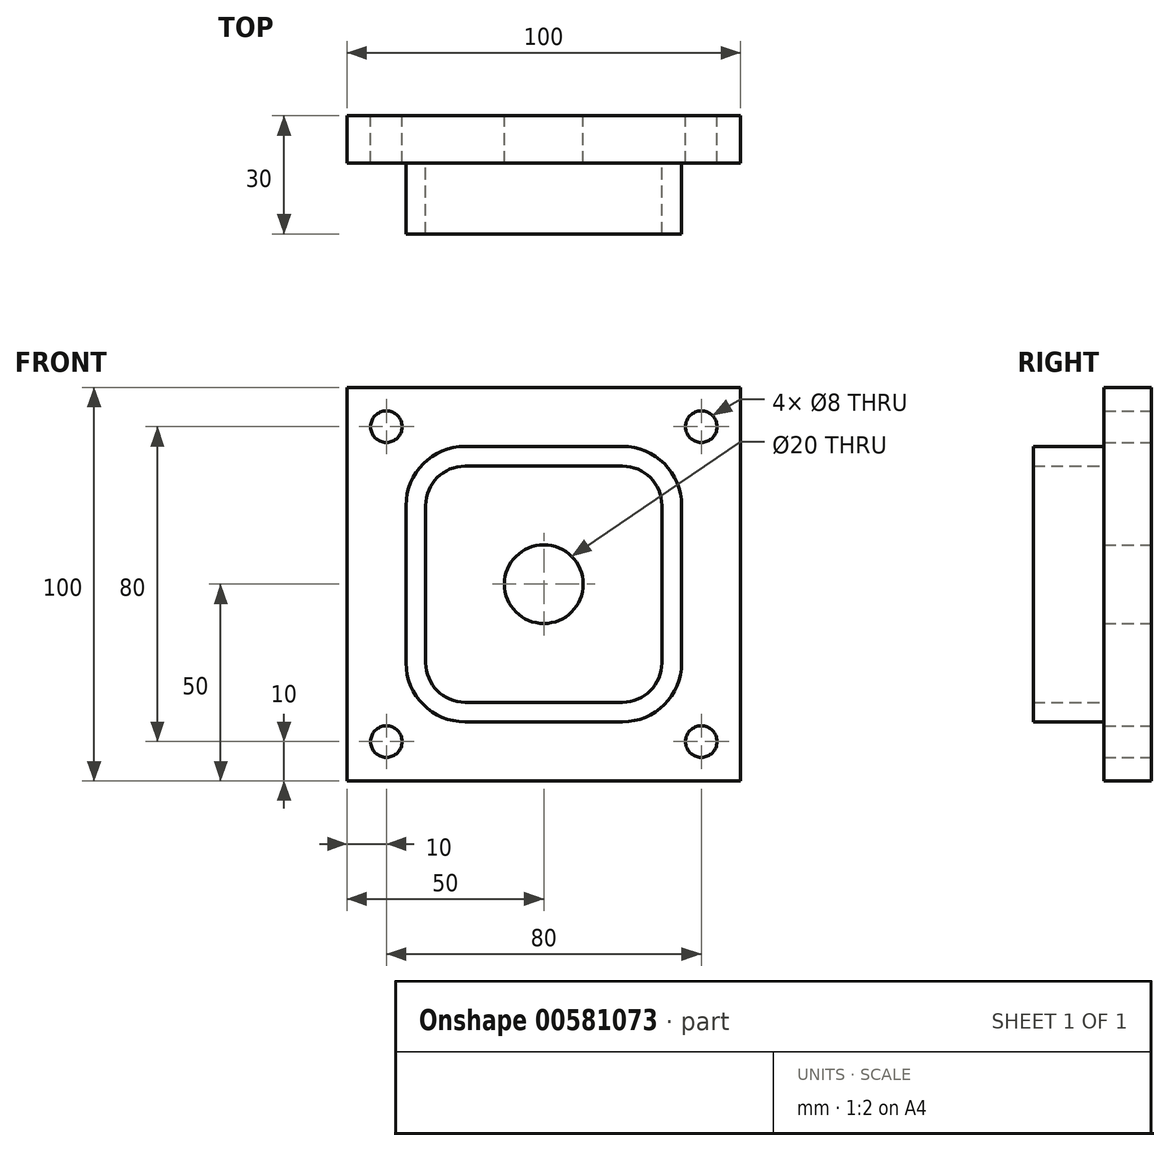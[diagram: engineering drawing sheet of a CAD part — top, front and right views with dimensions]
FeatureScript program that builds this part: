
annotation { "Feature Type Name" : "Feature", "Feature Type Description" : "" }
export const myFeature = defineFeature(function(context is Context, id is Id, definition is map)
    precondition{}
    {
        {
            var Q0;
            Q0=qCreatedBy(makeId("Front.planeOp"),FACE);
            var sketch = newSketch(context, id + "F0", { "sketchPlane" : qUnion([Q0])});
            skLineSegment(sketch, "E0", {"start": v(0, 47.7) * mm, "end": v(0, -43.35) * mm, "construction": true});
            skLineSegment(sketch, "E1", {"start": v(-44.12, 0) * mm, "end": v(43.1, 0) * mm, "construction": true});
            skLineSegment(sketch, "E2", {"start": v(-50, 50) * mm, "end": v(-50, -50) * mm});
            skLineSegment(sketch, "E3", {"start": v(-50, -50) * mm, "end": v(50, -50) * mm});
            skLineSegment(sketch, "E4", {"start": v(50, -50) * mm, "end": v(50, 50) * mm});
            skLineSegment(sketch, "E5", {"start": v(50, 50) * mm, "end": v(-50, 50) * mm});
            skLineSegment(sketch, "E6", {"start": v(-40, -37.93) * mm, "end": v(-40, -42.07) * mm, "construction": true});
            skLineSegment(sketch, "E7", {"start": v(-44.86, -40) * mm, "end": v(-37.72, -40) * mm, "construction": true});
            skPoint(sketch, "E7.startSnap0", {"position": v(-40, -40) * mm});
            skCircle(sketch, "E8", {"center": v(-40, -40) * mm, "radius": 4 * mm});
            skLineSegment(sketch, "E9", {"start": v(-35, 0) * mm, "end": v(-35, 20) * mm});
            skLineSegment(sketch, "E10", {"start": v(0, 35) * mm, "end": v(-20, 35) * mm});
            skArc(sketch, "E11", {"start": v(-20, 35) * mm, "mid": v(-30.6, 30.6) * mm, "end": v(-35, 20) * mm});
            skLineSegment(sketch, "E12", {"start": v(-30, 0) * mm, "end": v(-30, 20) * mm});
            skLineSegment(sketch, "E13", {"start": v(0, 30) * mm, "end": v(-20, 30) * mm});
            skArc(sketch, "E14", {"start": v(-20, 30) * mm, "mid": v(-27.07, 27.07) * mm, "end": v(-30, 20) * mm});
            skLineSegment(sketch, "E15.MirrorCS", {"start": v(0, 30) * mm, "end": v(20, 30) * mm});
            skLineSegment(sketch, "E16.MirrorCS", {"start": v(0, 35) * mm, "end": v(20, 35) * mm});
            skArc(sketch, "E17.MirrorCS", {"start": v(20, 35) * mm, "mid": v(30.6, 30.6) * mm, "end": v(35, 20) * mm});
            skArc(sketch, "E18.MirrorCS", {"start": v(20, 30) * mm, "mid": v(27.07, 27.07) * mm, "end": v(30, 20) * mm});
            skLineSegment(sketch, "E19.MirrorCS", {"start": v(30, 0) * mm, "end": v(30, 20) * mm});
            skLineSegment(sketch, "E20.MirrorCS", {"start": v(35, 0) * mm, "end": v(35, 20) * mm});
            skLineSegment(sketch, "E21.MirrorCS", {"start": v(-35, 0) * mm, "end": v(-35, -20) * mm});
            skArc(sketch, "E22.MirrorCS", {"start": v(-20, -35) * mm, "mid": v(-30.6, -30.6) * mm, "end": v(-35, -20) * mm});
            skArc(sketch, "E23.MirrorCS", {"start": v(-20, -30) * mm, "mid": v(-27.07, -27.07) * mm, "end": v(-30, -20) * mm});
            skLineSegment(sketch, "E24.MirrorCS", {"start": v(0, -35) * mm, "end": v(-20, -35) * mm});
            skLineSegment(sketch, "E25.MirrorCS", {"start": v(0, -30) * mm, "end": v(-20, -30) * mm});
            skLineSegment(sketch, "E26.MirrorCS", {"start": v(-30, 0) * mm, "end": v(-30, -20) * mm});
            skLineSegment(sketch, "E27.MirrorCS", {"start": v(0, -35) * mm, "end": v(20, -35) * mm});
            skLineSegment(sketch, "E28.MirrorCS", {"start": v(0, -30) * mm, "end": v(20, -30) * mm});
            skArc(sketch, "E29.MirrorCS", {"start": v(20, -35) * mm, "mid": v(30.6, -30.6) * mm, "end": v(35, -20) * mm});
            skArc(sketch, "E30.MirrorCS", {"start": v(20, -30) * mm, "mid": v(27.07, -27.07) * mm, "end": v(30, -20) * mm});
            skLineSegment(sketch, "E31.MirrorCS", {"start": v(30, 0) * mm, "end": v(30, -20) * mm});
            skLineSegment(sketch, "E32.MirrorCS", {"start": v(35, 0) * mm, "end": v(35, -20) * mm});
            skCircle(sketch, "E33", {"center": v(0, 0) * mm, "radius": 10 * mm});
            skCircle(sketch, "E34.MirrorC", {"center": v(40, -40) * mm, "radius": 4 * mm});
            skLineSegment(sketch, "E35.MirrorCS", {"start": v(44.86, -40) * mm, "end": v(37.72, -40) * mm, "construction": true});
            skLineSegment(sketch, "E36.MirrorCS", {"start": v(40, -37.93) * mm, "end": v(40, -42.07) * mm, "construction": true});
            skPoint(sketch, "E37.MirrorP", {"position": v(-40, 40) * mm});
            skCircle(sketch, "E38.MirrorC", {"center": v(-40, 40) * mm, "radius": 4 * mm});
            skLineSegment(sketch, "E39.MirrorCS", {"start": v(-40, 37.93) * mm, "end": v(-40, 42.07) * mm, "construction": true});
            skCircle(sketch, "E40.MirrorC", {"center": v(40, 40) * mm, "radius": 4 * mm});
            skSolve(sketch);
        }
        {
            var Q0;
            Q0=makeQuery(id+"F0.imprint","IMPRINT",FACE,{"disambiguationData":[TD([[makeQuery(id+"F0.imprint","IMPRINT",EDGE,{"derivedFrom":sQuery(id+"F0.wireOp",EDGE,"E2")}),1.0]])]});
            var Q1;
            Q1=makeQuery(id+"F0.imprint","IMPRINT",FACE,{"disambiguationData":[TD([[makeQuery(id+"F0.imprint","IMPRINT",EDGE,{"derivedFrom":sQuery(id+"F0.wireOp",EDGE,"E12")}),-1.0]])]});
            var Q2;
            Q2=makeQuery(id+"F0.imprint","IMPRINT",FACE,{"disambiguationData":[TD([[makeQuery(id+"F0.imprint","IMPRINT",EDGE,{"derivedFrom":sQuery(id+"F0.wireOp",EDGE,"E9")}),-1.0]])]});
            extrude(context, id + "F1", {"entities" : qUnion([Q0, Q1, Q2]), "depth" : 12 * mm, "offsetDistance" : 25 * mm});
        }
        {
            var Q0;
            Q0=makeQuery(id+"F0.imprint","IMPRINT",FACE,{"disambiguationData":[TD([[makeQuery(id+"F0.imprint","IMPRINT",EDGE,{"derivedFrom":sQuery(id+"F0.wireOp",EDGE,"E9")}),-1.0]])]});
            extrude(context, id + "F2", {"entities" : qUnion([Q0]), "operationType" : NewBodyOperationType.ADD, "depth" : 30 * mm, "offsetDistance" : 25 * mm});
        }
        {
            var Q0;
            Q0=makeQuery(id+"F0.imprint","IMPRINT",FACE,{"disambiguationData":[TD([[makeQuery(id+"F0.imprint","IMPRINT",EDGE,{"derivedFrom":sQuery(id+"F0.wireOp",EDGE,"E38.MirrorC")}),-1.0]])]});
            var Q1;
            Q1=makeQuery(id+"F0.imprint","IMPRINT",FACE,{"disambiguationData":[TD([[makeQuery(id+"F0.imprint","IMPRINT",EDGE,{"derivedFrom":sQuery(id+"F0.wireOp",EDGE,"E40.MirrorC")}),1.0]])]});
            var Q2;
            Q2=makeQuery(id+"F0.imprint","IMPRINT",FACE,{"disambiguationData":[TD([[makeQuery(id+"F0.imprint","IMPRINT",EDGE,{"derivedFrom":sQuery(id+"F0.wireOp",EDGE,"E8")}),1.0]])]});
            var Q3;
            Q3=makeQuery(id+"F0.imprint","IMPRINT",FACE,{"disambiguationData":[TD([[makeQuery(id+"F0.imprint","IMPRINT",EDGE,{"derivedFrom":sQuery(id+"F0.wireOp",EDGE,"E34.MirrorC")}),-1.0]])]});
            extrude(context, id + "F3", {"entities" : qUnion([Q0, Q1, Q2, Q3]), "operationType" : NewBodyOperationType.REMOVE, "oppositeDirection" : true, "depth" : 25 * mm, "offsetDistance" : 25 * mm});
        }
    });
